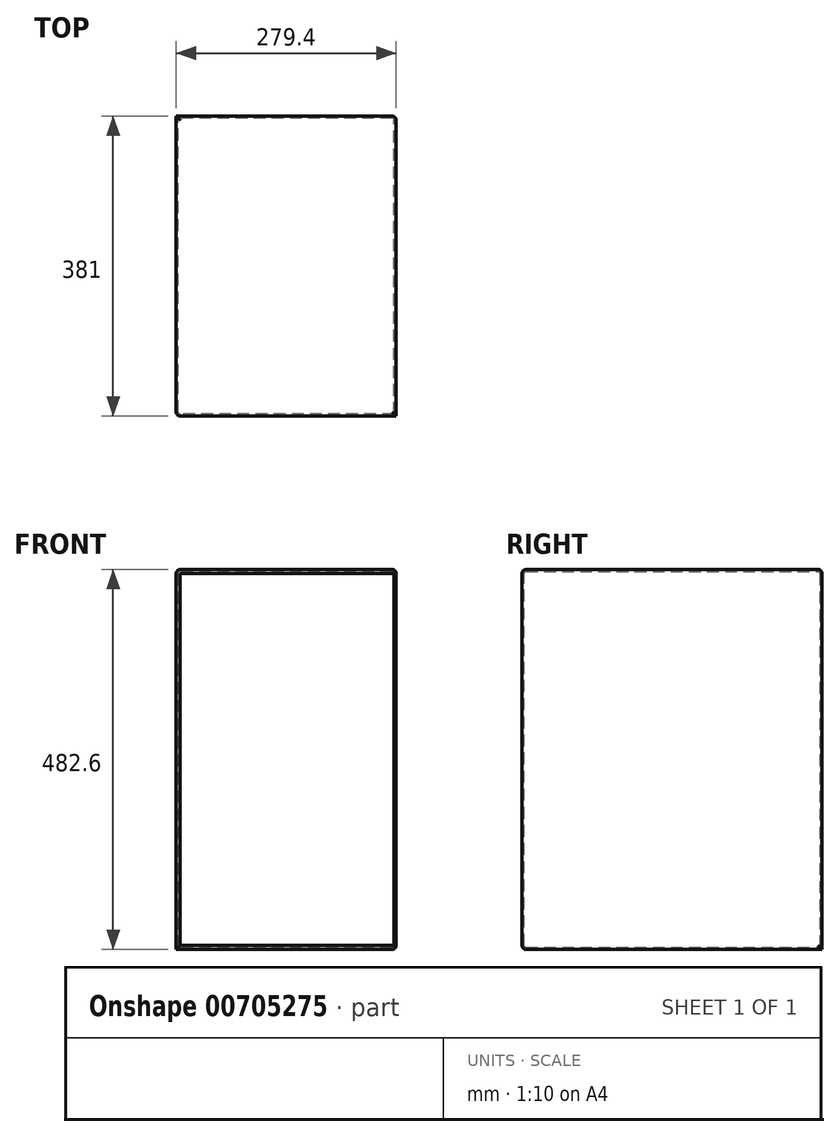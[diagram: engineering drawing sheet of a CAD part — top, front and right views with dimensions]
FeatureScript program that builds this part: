
annotation { "Feature Type Name" : "Feature", "Feature Type Description" : "" }
export const myFeature = defineFeature(function(context is Context, id is Id, definition is map)
    precondition{}
    {
        {
            var Q0;
            Q0=qCreatedBy(makeId("Front.planeOp"),FACE);
            var sketch = newSketch(context, id + "F0", { "sketchPlane" : qUnion([Q0])});
            skLineSegment(sketch, "E0.bottom", {"start": v(139.7, 241.3) * mm, "end": v(-139.7, 241.3) * mm});
            skLineSegment(sketch, "E0.top", {"start": v(139.7, -241.3) * mm, "end": v(-139.7, -241.3) * mm});
            skLineSegment(sketch, "E0.left", {"start": v(139.7, 241.3) * mm, "end": v(139.7, -241.3) * mm});
            skLineSegment(sketch, "E0.right", {"start": v(-139.7, 241.3) * mm, "end": v(-139.7, -241.3) * mm});
            skPoint(sketch, "E0.middle", {"position": v(0, 0) * mm});
            skSolve(sketch);
        }
        {
            var Q0;
            Q0=makeQuery(id+"F0.imprint","IMPRINT",FACE,{"disambiguationData":[TD([[makeQuery(id+"F0.imprint","IMPRINT",EDGE,{"derivedFrom":sQuery(id+"F0.wireOp",EDGE,"E0.bottom")}),1.0]])]});
            extrude(context, id + "F1", {"entities" : qUnion([Q0]), "depth" : 381 * mm, "offsetDistance" : 25.4 * mm});
        }
        {
            var Q0;
            Q0=makeQuery(id+"F1.opExtrude","SWEPT_EDGE",EDGE,{"disambiguationData":[OSD([sQuery(id+"F0.wireOp",EDGE,"E0.bottom"),sQuery(id+"F0.wireOp",EDGE,"E0.left")])]});
            var Q1;
            Q1=makeQuery(id+"F1.opExtrude","SWEPT_EDGE",EDGE,{"disambiguationData":[OSD([sQuery(id+"F0.wireOp",EDGE,"E0.bottom"),sQuery(id+"F0.wireOp",EDGE,"E0.right")])]});
            var Q2;
            Q2=makeQuery(id+"F1.opExtrude","SWEPT_EDGE",EDGE,{"disambiguationData":[OSD([sQuery(id+"F0.wireOp",EDGE,"E0.top"),sQuery(id+"F0.wireOp",EDGE,"E0.left")])]});
            var Q3;
            Q3=makeQuery(id+"F1.opExtrude","CAP_EDGE",EDGE,{"disambiguationData":[OSD([sQuery(id+"F0.wireOp",EDGE,"E0.left")])],"isStart":true});
            var Q4;
            Q4=makeQuery(id+"F1.opExtrude","CAP_EDGE",EDGE,{"disambiguationData":[OSD([sQuery(id+"F0.wireOp",EDGE,"E0.bottom")])],"isStart":true});
            var Q5;
            Q5=makeQuery(id+"F1.opExtrude","CAP_EDGE",EDGE,{"disambiguationData":[OSD([sQuery(id+"F0.wireOp",EDGE,"E0.right")])],"isStart":false});
            var Q6;
            Q6=makeQuery(id+"F1.opExtrude","CAP_EDGE",EDGE,{"disambiguationData":[OSD([sQuery(id+"F0.wireOp",EDGE,"E0.top")])],"isStart":false});
            var Q7;
            Q7=makeQuery(id+"F1.opExtrude","CAP_EDGE",EDGE,{"disambiguationData":[OSD([sQuery(id+"F0.wireOp",EDGE,"E0.bottom")])],"isStart":false});
            fillet(context, id + "F2", {"entities" : qUnion([Q0, Q1, Q2, Q3, Q4, Q5, Q6, Q7]), "radius" : 5 * mm, "tangentPropagation" : true, "allowEdgeOverflow" : false});
        }
        {
            var Q0;
            Q0=makeQuery(id+"F1.opExtrude","CAP_FACE",FACE,{"disambiguationData":[OSD([sQuery(id+"F0.wireOp",EDGE,"E0.bottom"),sQuery(id+"F0.wireOp",EDGE,"E0.top"),sQuery(id+"F0.wireOp",EDGE,"E0.left"),sQuery(id+"F0.wireOp",EDGE,"E0.right")])],"isStart":false});
            shell(context, id + "F3", {"entities" : qUnion([Q0]), "thickness" : 2.54 * mm});
        }
    });
